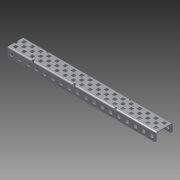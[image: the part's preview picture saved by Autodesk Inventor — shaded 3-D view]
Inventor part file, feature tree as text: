
AUTODESK INVENTOR PART (.ipt)
format: ipt  version: 2014 SP1 (Build 180222100, 222)  size: 1,440,256 bytes
history: native  units: in
note: dims shown in document units (in); Inventor stores cm internally (conversion verified against a paired STEP export)
features: other x1, imported_body x1, extrude x1, sketch x1
ambient origin geometry x8: Origin, YZ Plane, XZ Plane, XY Plane, X Axis, Y Axis, Z Axis, Center Point
bodies: Body1 (feature_tree)
feature tree (4):
  parser-record x1  (decoder bookkeeping rows leaked as tree rows — omitted from the tree; the rows remain in map.json)
  imported_body  "Base1"
  extrude  "Extrusion1"  Depth=1.0in TaperAngle=0.0deg
  sketch  "Sketch1"  dims[d1=3.5in d2=1.0in d3=0.0in]
